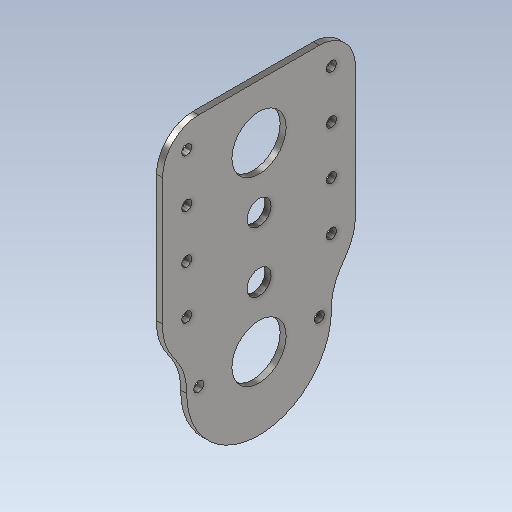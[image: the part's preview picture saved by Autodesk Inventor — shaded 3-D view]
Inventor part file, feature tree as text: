
AUTODESK INVENTOR PART (.ipt)
format: ipt  version: 2023 (Build 270158000, 158)  size: 199,168 bytes
history: native  units: in
note: dims shown in document units (in); Inventor stores cm internally (conversion verified against a paired STEP export)
features: extrude x1, fillet x1
ambient origin geometry x8: Origin, YZ Plane, XZ Plane, XY Plane, X Axis, Y Axis, Z Axis, Center Point
bodies: Solid1 (feature_tree)
feature tree (2):
  extrude  "Extrusion1"  Depth=4.0in
  fillet  "Fillet3"  Radius=6.0in
